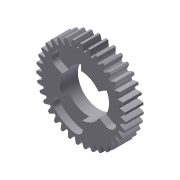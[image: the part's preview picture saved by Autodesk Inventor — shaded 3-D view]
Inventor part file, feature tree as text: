
AUTODESK INVENTOR PART (.ipt)
format: ipt  version: 2013 (Build 170138000, 138)  size: 356,352 bytes
history: native  units: mm (DEFAULTED — no unit token found)
features: sketch x4, extrude x3, plane x3, other x3, pattern_circular x1
ambient origin geometry x8: Origin, YZ Plane, XZ Plane, XY Plane, X Axis, Y Axis, Z Axis, Center Point
bodies: Solid1 (feature_tree)
feature tree (14):
  extrude  "Extrusion1"  Depth=9.525mm TaperAngle=0.0deg
  plane  "Work Plane1"
  plane  "Work Plane2"
  plane  "Work Plane3"
  other  "Spur Gear"
  extrude  "Extrusion4"  Depth=76.2mm TaperAngle=0.0deg
  extrude  "Extrusion5"  Depth=22.225mm
  pattern_circular  "Circular Pattern1"  [2 undecoded]
  sketch  "Sketch1"  dims[d0=46.99mm d1=9.525mm d2=0.0mm]
  sketch  "Sketch2"  dims[d3=44.45mm d4=76.2mm d5=0.0mm]
  other  "Srf1"
  sketch  "Sketch6"  dims[d6=0.0mm d7=0.897598mm d31=22.225mm]
  sketch  "Sketch7"  dims[d32=25.4mm d33=0.0mm d34=19.05mm d35=11.170107mm d36=3.81mm d37=3.6576mm d38=0.0mm d39=30.0mm d40=360.0deg]
  other  "Pitch Diameter"
note: 2 required parameter values undecoded (feature->parameter linkage not recoverable at this tier; creation-order binding heuristic only, values carry confidence <= 0.55)
